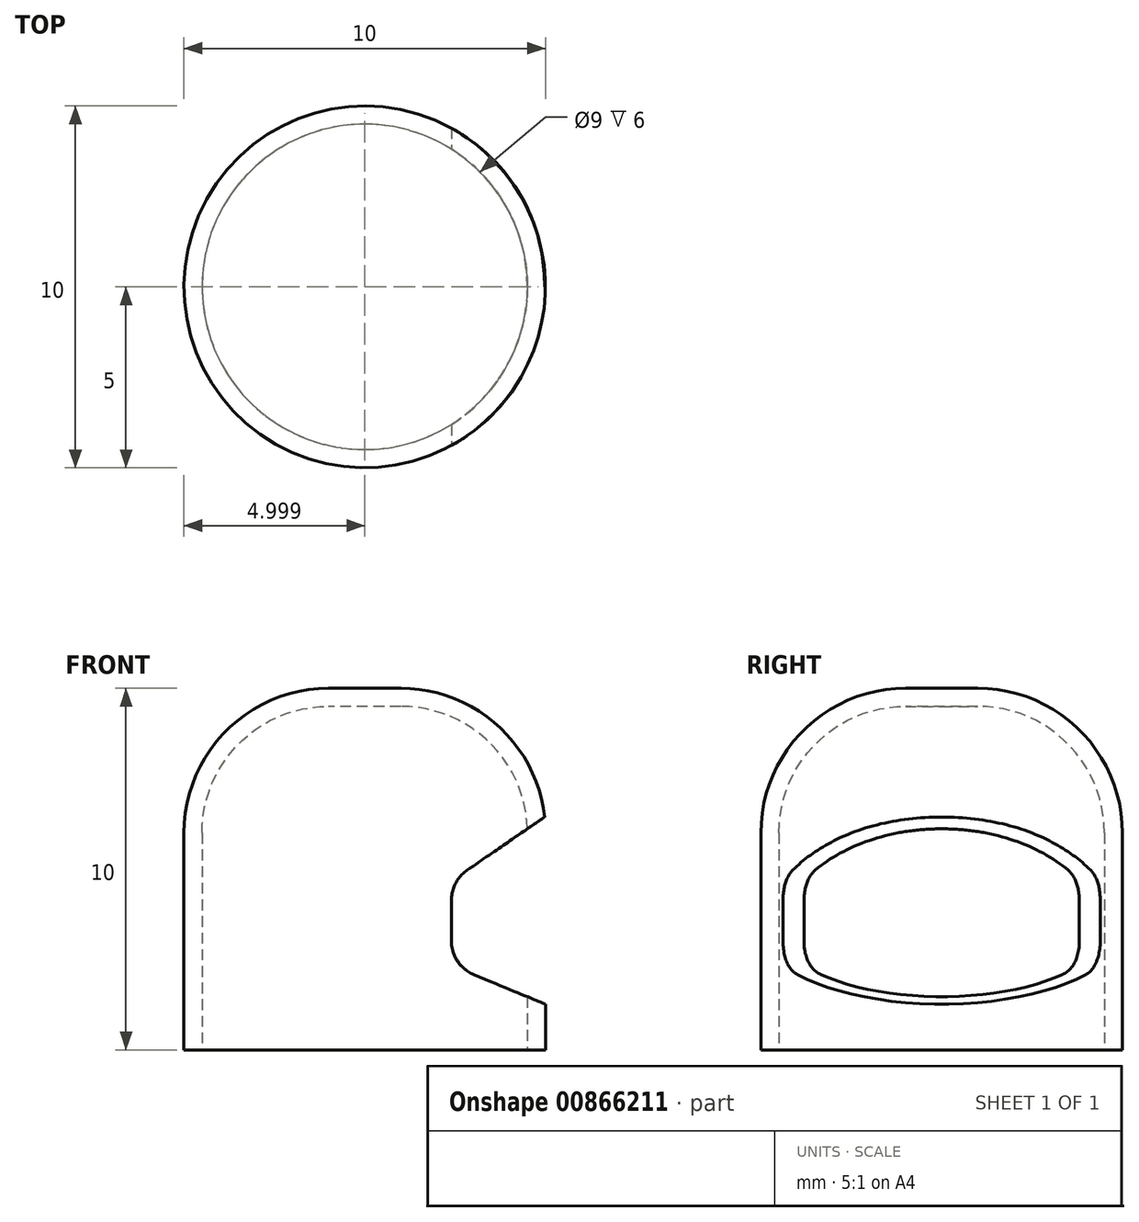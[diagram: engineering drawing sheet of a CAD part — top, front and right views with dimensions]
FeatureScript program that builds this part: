
annotation { "Feature Type Name" : "Feature", "Feature Type Description" : "" }
export const myFeature = defineFeature(function(context is Context, id is Id, definition is map)
    precondition{}
    {
        {
            var Q0;
            Q0=qCreatedBy(makeId("Top.planeOp"),FACE);
            var sketch = newSketch(context, id + "F0", { "sketchPlane" : qUnion([Q0])});
            skCircle(sketch, "E0", {"center": v(0.59, 0) * mm, "radius": 5 * mm});
            skSolve(sketch);
        }
        {
            var Q0;
            Q0 = qSketchRegion(id + "F0", true);
            extrude(context, id + "F1", {"entities" : qUnion([Q0]), "depth" : 10 * mm, "offsetDistance" : 25 * mm});
        }
        {
            var Q0;
            Q0=makeQuery(id+"F1.opExtrude","CAP_EDGE",EDGE,{"disambiguationData":[OSD([sQuery(id+"F0.wireOp",EDGE,"E0")])],"isStart":false});
            fillet(context, id + "F2", {"entities" : qUnion([Q0]), "radius" : 4 * mm, "tangentPropagation" : true, "allowEdgeOverflow" : false});
        }
        {
            var Q0;
            Q0=qCreatedBy(makeId("Front.planeOp"),FACE);
            var sketch = newSketch(context, id + "F3", { "sketchPlane" : qUnion([Q0])});
            skLineSegment(sketch, "E1", {"start": v(7.47, 7.74) * mm, "end": v(3.42, 4.97) * mm});
            skLineSegment(sketch, "E2", {"start": v(2.99, 4.15) * mm, "end": v(2.99, 3) * mm});
            skLineSegment(sketch, "E3", {"start": v(3.6, 2.08) * mm, "end": v(6.9, 0.73) * mm});
            skLineSegment(sketch, "E4", {"start": v(6.9, 0.73) * mm, "end": v(7.47, 7.74) * mm});
            skPoint(sketch, "E5.visualSharp", {"position": v(2.99, 4.67) * mm});
            skArc(sketch, "E5.filletArc", {"start": v(3.42, 4.97) * mm, "mid": v(3.1, 4.61) * mm, "end": v(2.99, 4.15) * mm});
            skPoint(sketch, "E6.visualSharp", {"position": v(2.99, 2.34) * mm});
            skArc(sketch, "E6.filletArc", {"start": v(2.99, 3) * mm, "mid": v(3.16, 2.45) * mm, "end": v(3.6, 2.08) * mm});
            skSolve(sketch);
        }
        {
            var Q0;
            Q0=makeQuery(id+"F1.opExtrude","CAP_FACE",FACE,{"disambiguationData":[OSD([sQuery(id+"F0.wireOp",EDGE,"E0")])],"isStart":true});
            shell(context, id + "F4", {"entities" : qUnion([Q0]), "thickness" : .5 * mm});
        }
        {
            var Q0;
            Q0=makeQuery(id+"F3.imprint","IMPRINT",FACE,{"disambiguationData":[TD([[makeQuery(id+"F3.imprint","IMPRINT",EDGE,{"derivedFrom":sQuery(id+"F3.wireOp",EDGE,"E1")}),1.0]])]});
            extrude(context, id + "F5", {"entities" : qUnion([Q0]), "operationType" : NewBodyOperationType.REMOVE, "endBound" : BoundingType.SYMMETRIC, "oppositeDirection" : true, "depth" : 25 * mm, "offsetDistance" : 25 * mm});
        }
    });
